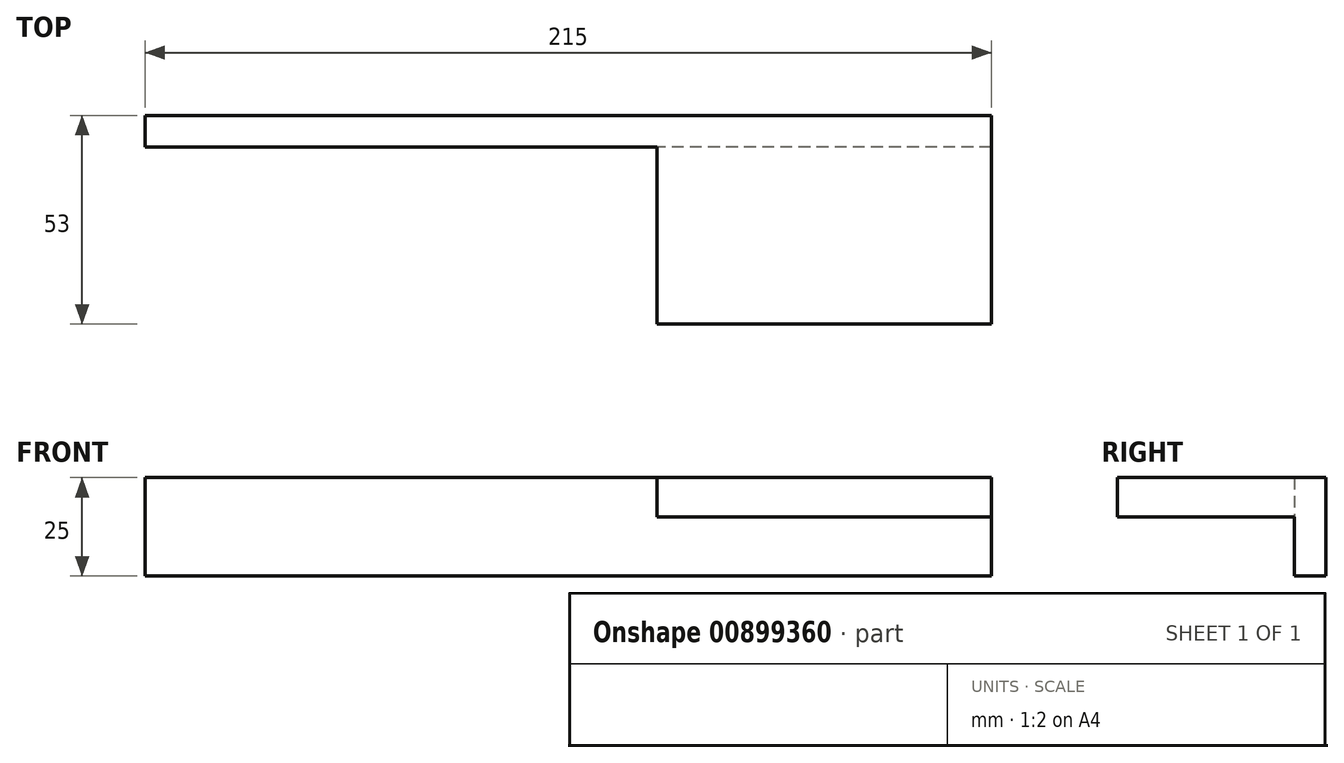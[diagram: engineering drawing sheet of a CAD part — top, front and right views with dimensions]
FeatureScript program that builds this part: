
annotation { "Feature Type Name" : "Feature", "Feature Type Description" : "" }
export const myFeature = defineFeature(function(context is Context, id is Id, definition is map)
    precondition{}
    {
        {
            var Q0;
            Q0=qCreatedBy(makeId("Front.planeOp"),FACE);
            var sketch = newSketch(context, id + "F0", { "sketchPlane" : qUnion([Q0])});
            skLineSegment(sketch, "E0.bottom", {"start": v(107.5, -12.5) * mm, "end": v(-107.5, -12.5) * mm});
            skLineSegment(sketch, "E0.top", {"start": v(107.5, 12.5) * mm, "end": v(-107.5, 12.5) * mm});
            skLineSegment(sketch, "E0.left", {"start": v(107.5, -12.5) * mm, "end": v(107.5, 12.5) * mm});
            skLineSegment(sketch, "E0.right", {"start": v(-107.5, -12.5) * mm, "end": v(-107.5, 12.5) * mm});
            skPoint(sketch, "E0.middle", {"position": v(0, 0) * mm});
            skLineSegment(sketch, "E1", {"start": v(107.5, -12.5) * mm, "end": v(22.5, -12.5) * mm, "construction": true});
            skSolve(sketch);
        }
        {
            var Q0;
            Q0=makeQuery(id+"F0.imprint","IMPRINT",FACE,{"disambiguationData":[TD([[makeQuery(id+"F0.imprint","IMPRINT",EDGE,{"derivedFrom":sQuery(id+"F0.wireOp",EDGE,"E0.bottom")}),-1.0]])]});
            extrude(context, id + "F1", {"entities" : qUnion([Q0]), "depth" : 8 * mm, "offsetDistance" : 25 * mm});
        }
        {
            var Q0;
            Q0=makeQuery(id+"F1.opExtrude","CAP_FACE",FACE,{"disambiguationData":[OSD([sQuery(id+"F0.wireOp",EDGE,"E0.bottom"),sQuery(id+"F0.wireOp",EDGE,"E0.top"),sQuery(id+"F0.wireOp",EDGE,"E0.left"),sQuery(id+"F0.wireOp",EDGE,"E0.right")])],"isStart":false});
            var sketch = newSketch(context, id + "F2", { "sketchPlane" : qUnion([Q0])});
            skLineSegment(sketch, "E2.bottom", {"start": v(107.5, 12.5) * mm, "end": v(22.5, 12.5) * mm});
            skLineSegment(sketch, "E2.top", {"start": v(107.5, 2.5) * mm, "end": v(22.5, 2.5) * mm});
            skLineSegment(sketch, "E2.left", {"start": v(107.5, 12.5) * mm, "end": v(107.5, 2.5) * mm});
            skLineSegment(sketch, "E2.right", {"start": v(22.5, 12.5) * mm, "end": v(22.5, 2.5) * mm});
            skSolve(sketch);
        }
        {
            var Q0;
            Q0 = qSketchRegion(id + "F2", true);
            extrude(context, id + "F3", {"entities" : qUnion([Q0]), "operationType" : NewBodyOperationType.ADD, "depth" : 45 * mm, "offsetDistance" : 25 * mm});
        }
    });
